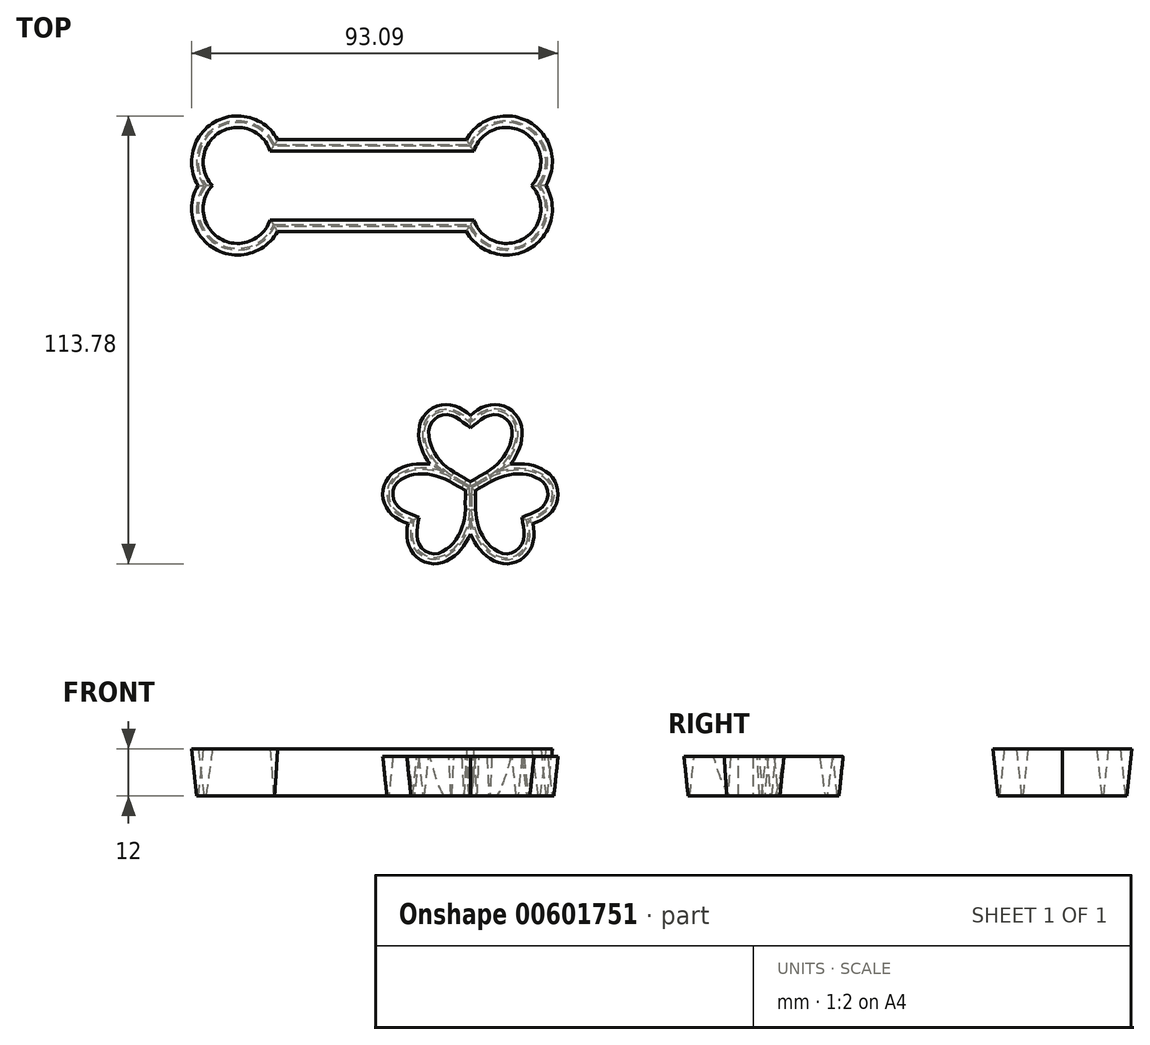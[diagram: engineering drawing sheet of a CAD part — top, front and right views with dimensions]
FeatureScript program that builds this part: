
annotation { "Feature Type Name" : "Feature", "Feature Type Description" : "" }
export const myFeature = defineFeature(function(context is Context, id is Id, definition is map)
    precondition{}
    {
        {
            var Q0;
            Q0=qCreatedBy(makeId("Top.planeOp"),FACE);
            var sketch = newSketch(context, id + "F0", { "sketchPlane" : qUnion([Q0])});
            skFitSpline(sketch, "E0", {"points": [v(0, 0) * mm, v(-6.18, 3.1) * mm, v(-11.32, 9.04) * mm, v(-12.35, 13.6) * mm, v(-8.98, 18.2) * mm, v(-3.64, 17.85) * mm, v(0, 14.57) * mm], "startDerivative": vector(-34.98, 13.49) * mm, "endDerivative": vector(20.93, -24.42) * mm});
            skFitSpline(sketch, "E1.MirrorCS", {"points": [v(0, 0) * mm, v(6.18, 3.1) * mm, v(11.32, 9.04) * mm, v(12.35, 13.6) * mm, v(8.98, 18.2) * mm, v(3.64, 17.85) * mm, v(0, 14.57) * mm], "startDerivative": vector(34.98, 13.49) * mm, "endDerivative": vector(-20.93, -24.42) * mm});
            skFitSpline(sketch, "E2", {"points": [v(0, -56.94) * mm, v(-4.57, -54.79) * mm, v(-9.81, -49.14) * mm, v(-11.83, -41.87) * mm, v(-7.26, -36.63) * mm, v(-1.88, -38.24) * mm, v(0, -40.4) * mm], "startDerivative": vector(-29.4, 10.65) * mm, "endDerivative": vector(12.34, -18.3) * mm});
            skFitSpline(sketch, "E3.MirrorCS", {"points": [v(0, -56.94) * mm, v(4.57, -54.79) * mm, v(9.81, -49.14) * mm, v(11.83, -41.87) * mm, v(7.26, -36.63) * mm, v(1.88, -38.24) * mm, v(0, -40.4) * mm], "startDerivative": vector(29.4, 10.65) * mm, "endDerivative": vector(-12.34, -18.3) * mm});
            skFitSpline(sketch, "E4", {"points": [v(0, -31.42) * mm, v(-5.74, -28.06) * mm, v(-10.58, -22.4) * mm, v(-10.99, -15) * mm, v(-5.74, -12.19) * mm, v(0, -15.28) * mm], "startDerivative": vector(-29.61, 15.21) * mm, "endDerivative": vector(27.92, -22.67) * mm});
            skFitSpline(sketch, "E5.MirrorCS", {"points": [v(0, -31.42) * mm, v(5.74, -28.06) * mm, v(10.58, -22.4) * mm, v(10.99, -15) * mm, v(5.74, -12.19) * mm, v(0, -15.28) * mm], "startDerivative": vector(29.61, 15.21) * mm, "endDerivative": vector(-27.92, -22.67) * mm});
            skFitSpline(sketch, "E6.0", {"points": [v(0.18, -31.78) * mm, v(0.8, -31.46) * mm, v(2.04, -30.82) * mm, v(3.88, -29.8) * mm, v(5.69, -28.63) * mm, v(7.44, -27.26) * mm, v(9.05, -25.63) * mm, v(10.2, -24.05) * mm, v(10.94, -22.63) * mm, v(11.57, -21.1) * mm, v(11.97, -19.48) * mm, v(12.08, -17.87) * mm, v(11.99, -16.68) * mm, v(11.71, -15.56) * mm, v(11.22, -14.53) * mm, v(10.5, -13.64) * mm, v(9.35, -12.66) * mm, v(7.97, -12.02) * mm, v(6.5, -11.76) * mm, v(5.41, -11.78) * mm, v(4.37, -12.01) * mm, v(3.05, -12.55) * mm, v(1.5, -13.54) * mm, v(0.33, -14.5) * mm, v(-0.25, -14.97) * mm]});
            skFitSpline(sketch, "E6.1", {"points": [v(-0.18, -31.78) * mm, v(-0.8, -31.46) * mm, v(-2.04, -30.82) * mm, v(-3.88, -29.8) * mm, v(-5.69, -28.63) * mm, v(-7.44, -27.26) * mm, v(-9.05, -25.63) * mm, v(-10.2, -24.05) * mm, v(-10.94, -22.63) * mm, v(-11.57, -21.1) * mm, v(-11.97, -19.48) * mm, v(-12.08, -17.87) * mm, v(-11.99, -16.68) * mm, v(-11.71, -15.56) * mm, v(-11.22, -14.53) * mm, v(-10.5, -13.64) * mm, v(-9.35, -12.66) * mm, v(-7.97, -12.02) * mm, v(-6.5, -11.76) * mm, v(-5.41, -11.78) * mm, v(-4.37, -12.01) * mm, v(-3.05, -12.55) * mm, v(-1.5, -13.54) * mm, v(-0.33, -14.5) * mm, v(0.25, -14.97) * mm]});
            skLineSegment(sketch, "E7", {"start": v(-0.18, -31.78) * mm, "end": v(2.27, -33.03) * mm});
            skLineSegment(sketch, "E8.MirrorCS", {"start": v(0.18, -31.78) * mm, "end": v(-2.27, -33.03) * mm});
            skSolve(sketch);
        }
        {
            var Q0;
            Q0=makeQuery(id+"F0.imprint","IMPRINT",FACE,{"disambiguationData":[TD([[makeQuery(id+"F0.imprint","IMPRINT",EDGE,{"derivedFrom":sQuery(id+"F0.wireOp",EDGE,"E4")}),1.0]])]});
            extrude(context, id + "F1", {"entities" : qUnion([Q0]), "depth" : 10 * mm, "offsetDistance" : 25 * mm, "hasDraft" : true, "draftAngle" : 6 * degree});
        }
        {
            var Q0;
            Q0=makeQuery(id+"F1.opExtrude","CAP_FACE",FACE,{"disambiguationData":[OSD([sQuery(id+"F0.wireOp",EDGE,"E4"),sQuery(id+"F0.wireOp",EDGE,"E5.MirrorCS"),sQuery(id+"F0.wireOp",EDGE,"E6.0"),sQuery(id+"F0.wireOp",EDGE,"E6.1"),sQuery(id+"F0.wireOp",EDGE,"E7"),sQuery(id+"F0.wireOp",EDGE,"E8.MirrorCS")])],"isStart":true});
            var sketch = newSketch(context, id + "F2", { "sketchPlane" : qUnion([Q0])});
            skLineSegment(sketch, "E9", {"start": v(0, 31.42) * mm, "end": v(0, 31.87) * mm});
            skPoint(sketch, "E10", {"position": v(0, 31.64) * mm});
            skLineSegment(sketch, "E11", {"start": v(0, 31.74) * mm, "end": v(-0.18, 31.74) * mm});
            skSolve(sketch);
        }
        {
            var Q0;
            Q0=sQuery(id+"F2.wireOp",EDGE,"E11");
            cPlane(context, id + "F3", {"entities" : qUnion([Q0]), "cplaneType" : CPlaneType.LINE_ANGLE, "offset" : 25 * mm, "angle" : 0 * degree, "width" : 150 * mm, "height" : 150 * mm});
        }
        {
            var Q0;
            Q0=qCreatedBy(id+"F3.planeOp",FACE);
            var sketch = newSketch(context, id + "F4", { "sketchPlane" : qUnion([Q0])});
            skLineSegment(sketch, "E12", {"start": v(0, -3.7) * mm, "end": v(0, -3.24) * mm});
            skSolve(sketch);
        }
        {
            var Q0;
            Q0=makeQuery(id+"F1.opExtrude","SWEPT_BODY",BODY,{"disambiguationData":[OSD([sQuery(id+"F0.wireOp",EDGE,"E4"),sQuery(id+"F0.wireOp",EDGE,"E5.MirrorCS"),sQuery(id+"F0.wireOp",EDGE,"E6.0"),sQuery(id+"F0.wireOp",EDGE,"E6.1"),sQuery(id+"F0.wireOp",EDGE,"E7"),sQuery(id+"F0.wireOp",EDGE,"E8.MirrorCS")])]});
            var Q1;
            Q1=sQuery(id+"F4.wireOp",EDGE,"E12");
            circularPattern(context, id + "F5", {"operationType" : NewBodyOperationType.ADD, "entities" : qUnion([Q0]), "axis" : qUnion([Q1]), "angle" : 360 * degree, "instanceCount" : 3, "equalSpace" : true});
        }
        {
            var Q0;
            Q0=qCreatedBy(makeId("Top.planeOp"), FACE);
            var sketch = newSketch(context, id + "F6", { "sketchPlane" : qUnion([Q0])});
            skLineSegment(sketch, "E13", {"start": v(-50, 55) * mm, "end": v(0, 55) * mm});
            skLineSegment(sketch, "E14", {"start": v(0, 35) * mm, "end": v(-50, 35) * mm});
            skLineSegment(sketch, "E15", {"start": v(40.36, 45) * mm, "end": v(-74.18, 45) * mm, "construction": true});
            skArc(sketch, "E16", {"start": v(-50, 55) * mm, "mid": v(-64.2, 59.64) * mm, "end": v(-67.17, 45) * mm});
            skArc(sketch, "E17.MirrorC", {"start": v(-50, 35) * mm, "mid": v(-64.2, 30.36) * mm, "end": v(-67.17, 45) * mm});
            skLineSegment(sketch, "E18", {"start": v(-25, 72.83) * mm, "end": v(-25, 25.19) * mm, "construction": true});
            skArc(sketch, "E19.MirrorCS", {"start": v(0, 55) * mm, "mid": v(14.2, 59.64) * mm, "end": v(17.17, 45) * mm});
            skArc(sketch, "E20.MirrorCS", {"start": v(0, 35) * mm, "mid": v(14.2, 30.36) * mm, "end": v(17.17, 45) * mm});
            skArc(sketch, "E21.0", {"start": v(-0.26, 55.4) * mm, "mid": v(14.39, 60) * mm, "end": v(17.66, 45) * mm});
            skArc(sketch, "E21.1", {"start": v(-0.26, 34.6) * mm, "mid": v(14.39, 30) * mm, "end": v(17.66, 45) * mm});
            skLineSegment(sketch, "E21.2", {"start": v(-0.26, 34.6) * mm, "end": v(-49.74, 34.6) * mm});
            skArc(sketch, "E21.3", {"start": v(-49.74, 34.6) * mm, "mid": v(-64.39, 30) * mm, "end": v(-67.66, 45) * mm});
            skArc(sketch, "E21.4", {"start": v(-49.74, 55.4) * mm, "mid": v(-64.39, 60) * mm, "end": v(-67.66, 45) * mm});
            skLineSegment(sketch, "E21.5", {"start": v(-49.74, 55.4) * mm, "end": v(-0.26, 55.4) * mm});
            skSolve(sketch);
        }
        {
            var Q0;
            Q0 = qSketchRegion(id + "F6", true);
            extrude(context, id + "F7", {"entities" : qUnion([Q0]), "domain" : OperationDomain.MODEL, "flatOperationType" : FlatOperationType.REMOVE, "depth" : 12 * mm, "offsetDistance" : 25 * mm, "hasDraft" : true, "draftAngle" : 6 * degree});
        }
    });
